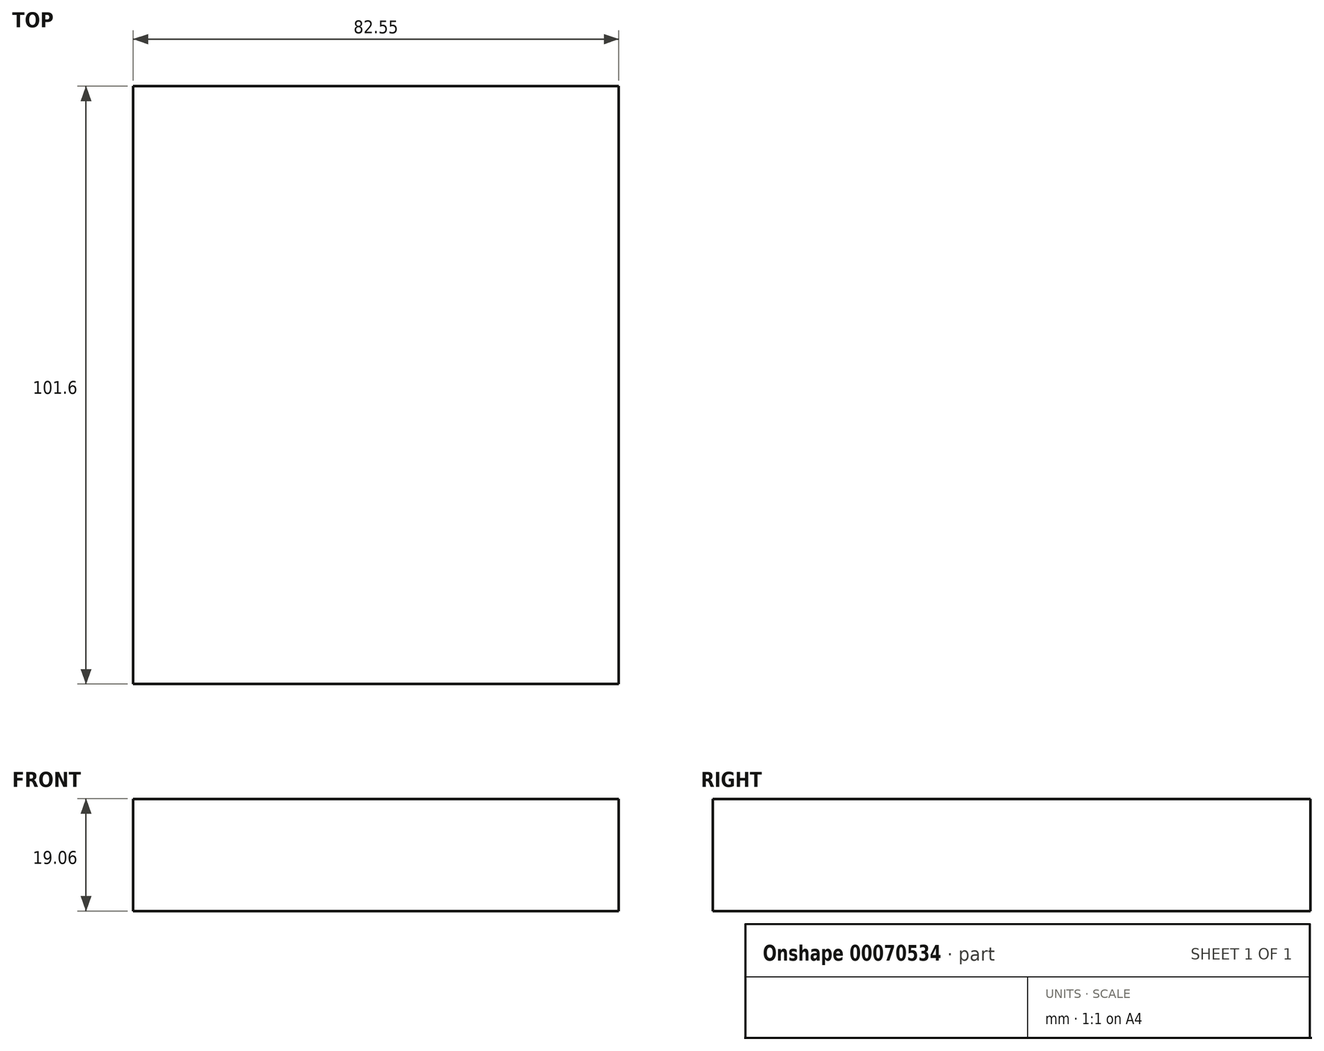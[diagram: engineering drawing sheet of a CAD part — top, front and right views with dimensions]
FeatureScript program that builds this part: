
annotation { "Feature Type Name" : "Feature", "Feature Type Description" : "" }
export const myFeature = defineFeature(function(context is Context, id is Id, definition is map)
    precondition{}
    {
        {
            var Q0;
            Q0=qCreatedBy(makeId("Front.planeOp"),FACE);
            var sketch = newSketch(context, id + "F0", { "sketchPlane" : qUnion([Q0])});
            skLineSegment(sketch, "E0.rect.bottom", {"start": v(41.27, 9.53) * mm, "end": v(-41.28, 9.53) * mm});
            skLineSegment(sketch, "E0.rect.top", {"start": v(41.28, -9.52) * mm, "end": v(-41.28, -9.52) * mm});
            skLineSegment(sketch, "E0.rect.left", {"start": v(41.28, 9.53) * mm, "end": v(41.28, -9.52) * mm});
            skLineSegment(sketch, "E0.rect.right", {"start": v(-41.28, 9.53) * mm, "end": v(-41.28, -9.52) * mm});
            skPoint(sketch, "E0.rect.middle", {"position": v(0, 0) * mm});
            skLineSegment(sketch, "E1.rect.bottom", {"start": v(111.13, 38.1) * mm, "end": v(60.33, 38.1) * mm});
            skLineSegment(sketch, "E1.rect.top", {"start": v(111.12, 66.67) * mm, "end": v(60.33, 66.67) * mm});
            skLineSegment(sketch, "E1.rect.left", {"start": v(111.12, 38.1) * mm, "end": v(111.12, 66.68) * mm});
            skLineSegment(sketch, "E1.rect.right", {"start": v(60.33, 38.1) * mm, "end": v(60.33, 66.68) * mm});
            skPoint(sketch, "E1.rect.middle", {"position": v(85.73, 52.39) * mm});
            skLineSegment(sketch, "E2", {"start": v(41.27, 9.53) * mm, "end": v(41.27, 27) * mm});
            skArc(sketch, "E3", {"start": v(41.28, 27) * mm, "mid": v(45.92, 38.23) * mm, "end": v(57.15, 42.88) * mm});
            skLineSegment(sketch, "E4", {"start": v(57.15, 42.88) * mm, "end": v(85.74, 42.88) * mm});
            skLineSegment(sketch, "E5.0", {"start": v(57.15, 61.93) * mm, "end": v(86.03, 61.93) * mm});
            skArc(sketch, "E5.1", {"start": v(22.23, 27) * mm, "mid": v(32.45, 51.7) * mm, "end": v(57.15, 61.93) * mm});
            skLineSegment(sketch, "E5.2", {"start": v(22.23, 9.53) * mm, "end": v(22.23, 27) * mm});
            skLineSegment(sketch, "E6", {"start": v(85.74, 42.88) * mm, "end": v(86.03, 61.93) * mm});
            skFitSpline(sketch, "E7", {"points": [v(-41.28, 9.52) * mm, v(57.15, 61.93) * mm], "startDerivative": vector(3.04, 69.9) * mm, "endDerivative": vector(149.5, -7.85) * mm});
            skSolve(sketch);
        }
        {
            var Q0;
            Q0=makeQuery(id+"F0.imprint","IMPRINT",FACE,{"disambiguationData":[TD([[makeQuery(id+"F0.imprint","IMPRINT",EDGE,{"derivedFrom":sQuery(id+"F0.wireOp",EDGE,"E0.rect.top")}),-1.0]])]});
            extrude(context, id + "F1", {"entities" : qUnion([Q0]), "endBound" : BoundingType.SYMMETRIC, "depth" : 101.6 * mm});
        }
    });
